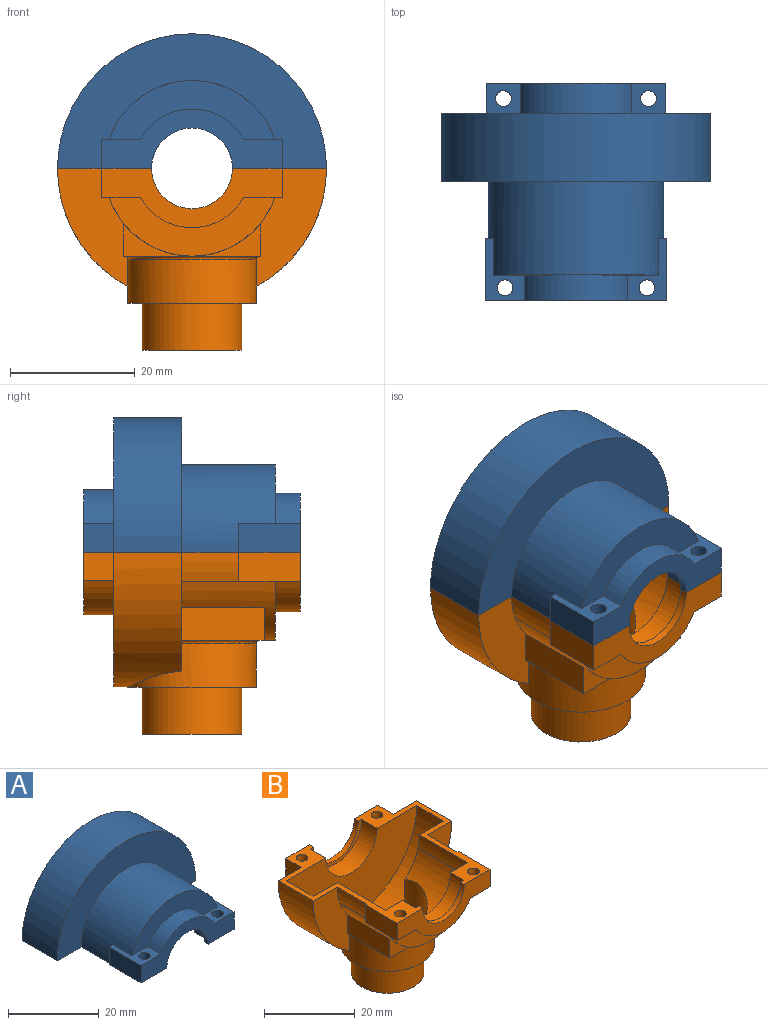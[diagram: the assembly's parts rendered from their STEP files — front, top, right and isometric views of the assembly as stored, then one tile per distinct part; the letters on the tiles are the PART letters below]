
ASSEMBLY  parts=2 mates=1
PART A: 36 faces, bbox 43.2x34.8x21.6 mm
  f0: plane 34.8x15.11mm, normal (0,0,-1), area 118.5mm2, adj f3,f4,f5,f6,f7,f8,f9,f11
  f1: plane 34.8x15.11mm, normal (0,0,-1), area 118.5mm2, adj f3,f4,f5,f6,f7,f8,f9,f11
  f2: plane 9.91x6.19mm, normal (0,0,1), area 27mm2, adj f3,f10,f13,f21,f22,f30,f35
  f3: cylinder r=14.1mm len=28.19mm, axis (0,-1,0), area 607.7mm2, adj f0,f1,f2,f10,f19,f29,f30,f31
  f4: cylinder r=12.83mm len=25.65mm, axis (0,-1,0), area 603.9mm2, adj f0,f1,f7,f28
  f5: plane 40.64x20.32mm, normal (0,-1,0), area 548mm2, adj f0,f1,f23,f26
  f6: cylinder r=6.99mm len=13.97mm, axis (0,-1,0), area 27.9mm2, adj f0,f1,f12,f27
  f7: plane 25.65x12.83mm, normal (0,1,0), area 170.3mm2, adj f0,f1,f4,f24
  f8: cylinder r=6.48mm len=12.95mm, axis (0,1,0), area 25.3mm2, adj f0,f1,f13,f25
  f9: cylinder r=21.59mm len=43.18mm, axis (0,1,0), area 740.8mm2, adj f0,f1,f11,f29
  f10: plane 26.58x9.4mm, normal (0,-1,0), area 125.4mm2, adj f2,f3,f19,f22
  f11: plane 43.18x21.59mm, normal (0,1,0), area 531.3mm2, adj f0,f1,f9,f14,f15,f16,f17,f18
  f12: plane 28.7x10.03mm, normal (0,1,0), area 124.2mm2, adj f0,f1,f6,f14,f15,f16,f17,f18
  f13: plane 28.96x9.53mm, normal (0,-1,0), area 126.9mm2, adj f0,f1,f2,f8,f19,f20,f21,f22
  f14: plane 5.42x4.83mm, normal (0,0,1), area 21.1mm2, adj f11,f12,f15,f18,f34
  f15: plane 4.83x4.57mm, normal (-1,0,0), area 22.1mm2, adj f1,f11,f12,f14
  f16: plane 4.83x4.57mm, normal (1,0,0), area 22.1mm2, adj f0,f11,f12,f17
  f17: plane 5.42x4.83mm, normal (0,0,1), area 21.1mm2, adj f11,f12,f16,f18,f33
  f18: cylinder r=10.03mm len=17.86mm, axis (0,1,0), area 106.3mm2, adj f11,f12,f14,f17
  f19: plane 9.91x6.19mm, normal (0,0,1), area 27mm2, adj f3,f10,f13,f20,f22,f31,f32
  f20: plane 9.91x4.7mm, normal (1,0,0), area 46.5mm2, adj f0,f13,f19,f31
  f21: plane 9.91x4.7mm, normal (-1,0,0), area 46.5mm2, adj f1,f2,f13,f30
  f22: cylinder r=9.53mm len=16.57mm, axis (0,-1,0), area 81.7mm2, adj f2,f10,f13,f19
  f23: cylinder r=20.32mm len=40.64mm, axis (0,1,0), area 535.1mm2, adj f0,f1,f5,f28
  f24: cylinder r=7.49mm len=14.99mm, axis (0,1,0), area 96.3mm2, adj f0,f1,f7,f25
  f25: plane 14.99x7.49mm, normal (0,1,0), area 22.3mm2, adj f0,f1,f8,f24
  f26: cylinder r=8mm len=16mm, axis (0,-1,0), area 121.3mm2, adj f0,f1,f5,f27
  f27: plane 16x8mm, normal (0,-1,0), area 23.9mm2, adj f0,f1,f6,f26
  f28: plane 40.64x20.32mm, normal (0,1,0), area 390.1mm2, adj f0,f1,f4,f23
  f29: plane 43.18x21.59mm, normal (0,-1,0), area 420mm2, adj f0,f1,f3,f9
  f30: plane 4.7x1.19mm, normal (0,1,0), area 3mm2, adj f1,f2,f3,f21
  f31: plane 4.7x1.19mm, normal (0,1,0), area 3mm2, adj f0,f3,f19,f20
  f32: cylinder r=1.27mm len=4.7mm, axis (0,0,1), area 37.5mm2, adj f0,f19
  f33: cylinder r=1.27mm len=4.57mm, axis (0,0,1), area 36.5mm2, adj f0,f17
  f34: cylinder r=1.27mm len=4.57mm, axis (0,0,1), area 36.5mm2, adj f1,f14
  f35: cylinder r=1.27mm len=4.7mm, axis (0,0,1), area 37.5mm2, adj f1,f2
PART B: 59 faces, bbox 43.2x34.8x29.2 mm
  f0: cylinder r=10.31mm len=20.62mm, axis (0,0,1), area 286.7mm2, adj f1,f2,f4,f57,f58
  f1: plane 19.07x11.44mm, normal (0,-1,0), area 124.9mm2, adj f0,f3,f4,f11,f20,f24,f43,f45
  f2: plane 19.07x11.44mm, normal (0,-1,0), area 124.9mm2, adj f0,f3,f4,f9,f21,f25,f42,f45
  f3: cylinder r=14.1mm len=26.58mm, axis (0,-1,0), area 190mm2, adj f1,f2,f17,f18,f20,f21,f42,f43
  f4: cylinder r=21.59mm len=43.18mm, axis (0,-1,0), area 603.8mm2, adj f0,f1,f2,f9,f11,f34
  f5: cylinder r=12.83mm len=24.72mm, axis (0,-1,0), area 315.5mm2, adj f6,f7,f12,f13,f14,f52
  f6: plane 18.56x12.06mm, normal (0,1,0), area 130mm2, adj f5,f8,f11,f14,f35,f52
  f7: plane 18.56x12.06mm, normal (0,1,0), area 130mm2, adj f5,f8,f9,f13,f15,f52
  f8: cylinder r=20.32mm len=40.64mm, axis (0,-1,0), area 576.9mm2, adj f6,f7,f9,f10,f11,f44,f52
  f9: plane 34.8x15.11mm, normal (0,0,1), area 118.5mm2, adj f2,f4,f7,f8,f10,f12,f15,f16
  f10: plane 40.64x20.32mm, normal (0,-1,0), area 548mm2, adj f8,f9,f11,f40
  f11: plane 34.8x15.11mm, normal (0,0,1), area 118.5mm2, adj f1,f4,f6,f8,f10,f12,f16,f22
  f12: plane 25.66x12.83mm, normal (0,1,0), area 170.3mm2, adj f5,f9,f11,f13,f14,f15,f35,f38
  f13: plane 14.99x0mm, normal (0,0,1), area 0.1mm2, adj f5,f7,f12,f15
  f14: plane 14.99x0mm, normal (0,0,1), area 0mm2, adj f5,f6,f12,f35
  f15: cylinder r=12.83mm len=14.99mm, axis (0,1,0), area 52mm2, adj f7,f9,f12,f13
  f16: plane 28.7x10.03mm, normal (0,1,0), area 124.2mm2, adj f9,f11,f29,f30,f31,f32,f33,f36
  f17: plane 21.84x5.21mm, normal (0,-1,0), area 35mm2, adj f3,f42,f43,f45
  f18: plane 26.58x9.4mm, normal (0,-1,0), area 125.4mm2, adj f3,f19,f20,f21
  f19: cylinder r=9.53mm len=16.57mm, axis (0,-1,0), area 81.7mm2, adj f18,f20,f21,f28
  f20: plane 19.05x6.19mm, normal (0,0,-1), area 27mm2, adj f1,f3,f18,f19,f22,f23,f24,f28
  f21: plane 19.05x6.19mm, normal (0,0,-1), area 27.1mm2, adj f2,f3,f18,f19,f25,f26,f27,f28
  f22: plane 9.91x4.7mm, normal (-1,0,0), area 46.5mm2, adj f11,f20,f23,f28
  f23: plane 4.7x1.19mm, normal (0,1,0), area 3mm2, adj f11,f20,f22,f24
  f24: cylinder r=14.1mm len=9.14mm, axis (0,1,0), area 43.8mm2, adj f1,f11,f20,f23
  f25: cylinder r=14.1mm len=9.14mm, axis (0,1,0), area 43.8mm2, adj f2,f9,f21,f26
  f26: plane 4.7x1.18mm, normal (0,1,0), area 3mm2, adj f9,f21,f25,f27
  f27: plane 9.91x4.7mm, normal (1,0,0), area 46.5mm2, adj f9,f21,f26,f28
  f28: plane 28.96x9.53mm, normal (0,-1,0), area 126.9mm2, adj f9,f11,f19,f20,f21,f22,f27,f37
  f29: plane 4.83x4.57mm, normal (-1,0,0), area 22.1mm2, adj f11,f16,f30,f34
  f30: plane 5.42x4.83mm, normal (0,0,-1), area 21.1mm2, adj f16,f29,f31,f34,f54
  f31: cylinder r=10.03mm len=17.86mm, axis (0,1,0), area 106.3mm2, adj f16,f30,f32,f34
  f32: plane 5.42x4.83mm, normal (0,0,-1), area 21.1mm2, adj f16,f31,f33,f34,f53
  f33: plane 4.83x4.57mm, normal (1,0,0), area 22.1mm2, adj f9,f16,f32,f34
  f34: plane 43.18x21.59mm, normal (0,1,0), area 531.3mm2, adj f4,f9,f11,f29,f30,f31,f32,f33
  f35: cylinder r=12.83mm len=14.99mm, axis (0,1,0), area 52mm2, adj f6,f11,f12,f14
  f36: cylinder r=6.99mm len=13.97mm, axis (0,1,0), area 27.9mm2, adj f9,f11,f16,f41
  f37: cylinder r=6.48mm len=12.95mm, axis (0,-1,0), area 25.3mm2, adj f9,f11,f28,f39
  f38: cylinder r=7.49mm len=14.99mm, axis (0,1,0), area 96.3mm2, adj f9,f11,f12,f39
  f39: plane 14.99x7.49mm, normal (0,1,0), area 22.3mm2, adj f9,f11,f37,f38
  f40: cylinder r=8mm len=16mm, axis (0,-1,0), area 121.3mm2, adj f9,f10,f11,f41
  f41: plane 16x8mm, normal (0,-1,0), area 23.9mm2, adj f9,f11,f36,f40
  f42: plane 13.21x5.21mm, normal (1,0,0), area 68.8mm2, adj f2,f3,f17,f45
  f43: plane 13.21x5.21mm, normal (-1,0,0), area 68.8mm2, adj f1,f3,f17,f45
  f44: cylinder r=6.48mm len=12.95mm, axis (0,0,1), area 72.1mm2, adj f8,f48
  f45: plane 21.84x13.21mm, normal (0,0,-1), area 69mm2, adj f1,f2,f17,f42,f43,f57
  f46: plane 12.95x12.95mm, normal (0,0,-1), area 58.6mm2, adj f47,f49
  f47: cylinder r=4.83mm len=9.65mm, axis (0,0,1), area 77mm2, adj f46,f48
  f48: plane 12.95x12.95mm, normal (0,0,1), area 58.6mm2, adj f44,f47
  f49: cylinder r=6.48mm len=12.95mm, axis (0,0,1), area 206.7mm2, adj f46,f51
  f50: cylinder r=8mm len=16mm, axis (0,0,1), area 378mm2, adj f51,f58
  f51: plane 16x16mm, normal (0,0,-1), area 69.3mm2, adj f49,f50
  f52: cylinder r=8.76mm len=17.53mm, axis (0,0,1), area 278mm2, adj f5,f6,f7,f8
  f53: cylinder r=1.27mm len=4.57mm, axis (0,0,-1), area 36.5mm2, adj f9,f32
  f54: cylinder r=1.27mm len=4.57mm, axis (0,0,-1), area 36.5mm2, adj f11,f30
  f55: cylinder r=1.27mm len=4.7mm, axis (0,0,-1), area 37.5mm2, adj f9,f21
  f56: cylinder r=1.27mm len=4.7mm, axis (0,0,-1), area 37.5mm2, adj f11,f20
  f57: torus R=10.82mm, axis (0,0,-1), area 28.9mm2, adj f0,f1,f2,f45
  f58: plane 20.62x20.62mm, normal (0,0,-1), area 133mm2, adj f0,f50
PLACE A t=(-29.5,31.77,65.64)mm
PLACE B t=(-29.5,14.37,15.08)mm
MATE fastened B.f11 <-> A.f1  axis (0,0,1) through (-43.85,31.77,65.64)mm
